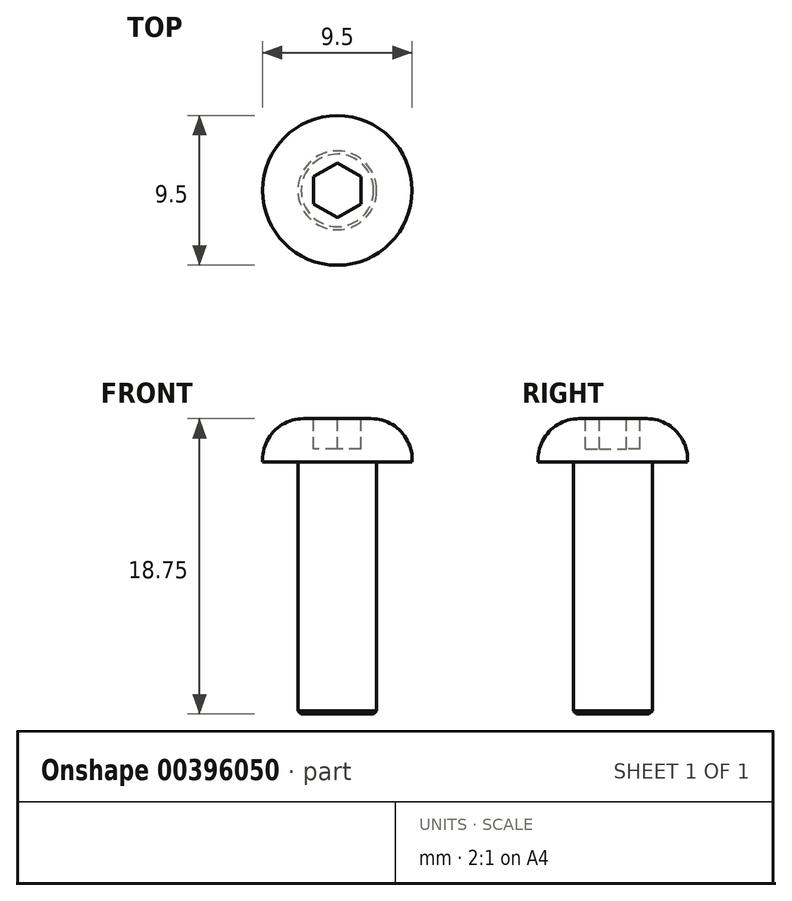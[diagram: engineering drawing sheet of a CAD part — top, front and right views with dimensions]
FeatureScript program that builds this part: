
annotation { "Feature Type Name" : "Feature", "Feature Type Description" : "" }
export const myFeature = defineFeature(function(context is Context, id is Id, definition is map)
    precondition{}
    {
        {
            var Q0;
            Q0=qCreatedBy(makeId("Top.planeOp"),FACE);
            var sketch = newSketch(context, id + "F0", { "sketchPlane" : qUnion([Q0])});
            skCircle(sketch, "E0", {"center": v(0, 0) * mm, "radius": 2.5 * mm});
            skSolve(sketch);
        }
        {
            var Q0;
            Q0=qSketchRegion(id+"F0",true);
            extrude(context, id + "F1", {"entities" : qUnion([Q0]), "oppositeDirection" : true, "depth" : 16 * mm});
        }
        {
            var Q0;
            Q0=makeQuery(id+"F1.opExtrude","CAP_EDGE",EDGE,{"disambiguationData":[OSD([sQuery(id+"F0.wireOp",EDGE,"E0")])],"isStart":false});
            chamfer(context, id + "F2", {"entities" : qUnion([Q0]), "chamferType" : ChamferType.OFFSET_ANGLE, "width" : 0.2 * mm, "oppositeDirection" : false, "angle" : 45 * degree, "tangentPropagation" : true});
        }
        {
            var Q0;
            Q0=makeQuery(id+"F1.opExtrude","CAP_FACE",FACE,{"disambiguationData":[OSD([sQuery(id+"F0.wireOp",EDGE,"E0")])],"isStart":true});
            var sketch = newSketch(context, id + "F3", { "sketchPlane" : qUnion([Q0])});
            skCircle(sketch, "E1", {"center": v(0, 0) * mm, "radius": 4.75 * mm});
            skSolve(sketch);
        }
        {
            var Q0;
            Q0=qSketchRegion(id+"F3",true);
            extrude(context, id + "F4", {"entities" : qUnion([Q0]), "operationType" : NewBodyOperationType.ADD, "depth" : 2.75 * mm});
        }
        {
            var Q0;
            Q0=makeQuery(id+"F4.opExtrude","CAP_FACE",FACE,{"disambiguationData":[OSD([sQuery(id+"F3.wireOp",EDGE,"E1")])],"isStart":false});
            var sketch = newSketch(context, id + "F5", { "sketchPlane" : qUnion([Q0])});
            skCircle(sketch, "E2.cCircle", {"center": v(0, 0) * mm, "radius": 1.5 * mm, "construction": true});
            skLineSegment(sketch, "E2.0", {"start": v(-1.5, -0.87) * mm, "end": v(-1.5, 0.87) * mm});
            skLineSegment(sketch, "E2.1", {"start": v(-1.5, 0.87) * mm, "end": v(0, 1.73) * mm});
            skLineSegment(sketch, "E2.2", {"start": v(0, 1.73) * mm, "end": v(1.5, 0.87) * mm});
            skLineSegment(sketch, "E2.3", {"start": v(1.5, 0.87) * mm, "end": v(1.5, -0.87) * mm});
            skLineSegment(sketch, "E2.4", {"start": v(1.5, -0.87) * mm, "end": v(0, -1.73) * mm});
            skLineSegment(sketch, "E2.5", {"start": v(0, -1.73) * mm, "end": v(-1.5, -0.87) * mm});
            skPoint(sketch, "E2.0.midPoint", {"position": v(-1.5, 0) * mm});
            skSolve(sketch);
        }
        {
            var Q0;
            Q0=qSketchRegion(id+"F5",true);
            extrude(context, id + "F6", {"entities" : qUnion([Q0]), "operationType" : NewBodyOperationType.REMOVE, "oppositeDirection" : true, "depth" : 1.92 * mm});
        }
        {
            var Q0;
            Q0=makeQuery(id+"F4.opExtrude","CAP_EDGE",EDGE,{"disambiguationData":[OSD([sQuery(id+"F3.wireOp",EDGE,"E1")])],"isStart":false});
            fillet(context, id + "F7", {"entities" : qUnion([Q0]), "radius" : (5.2 / 2) * mm, "allowEdgeOverflow" : false});
        }
    });
